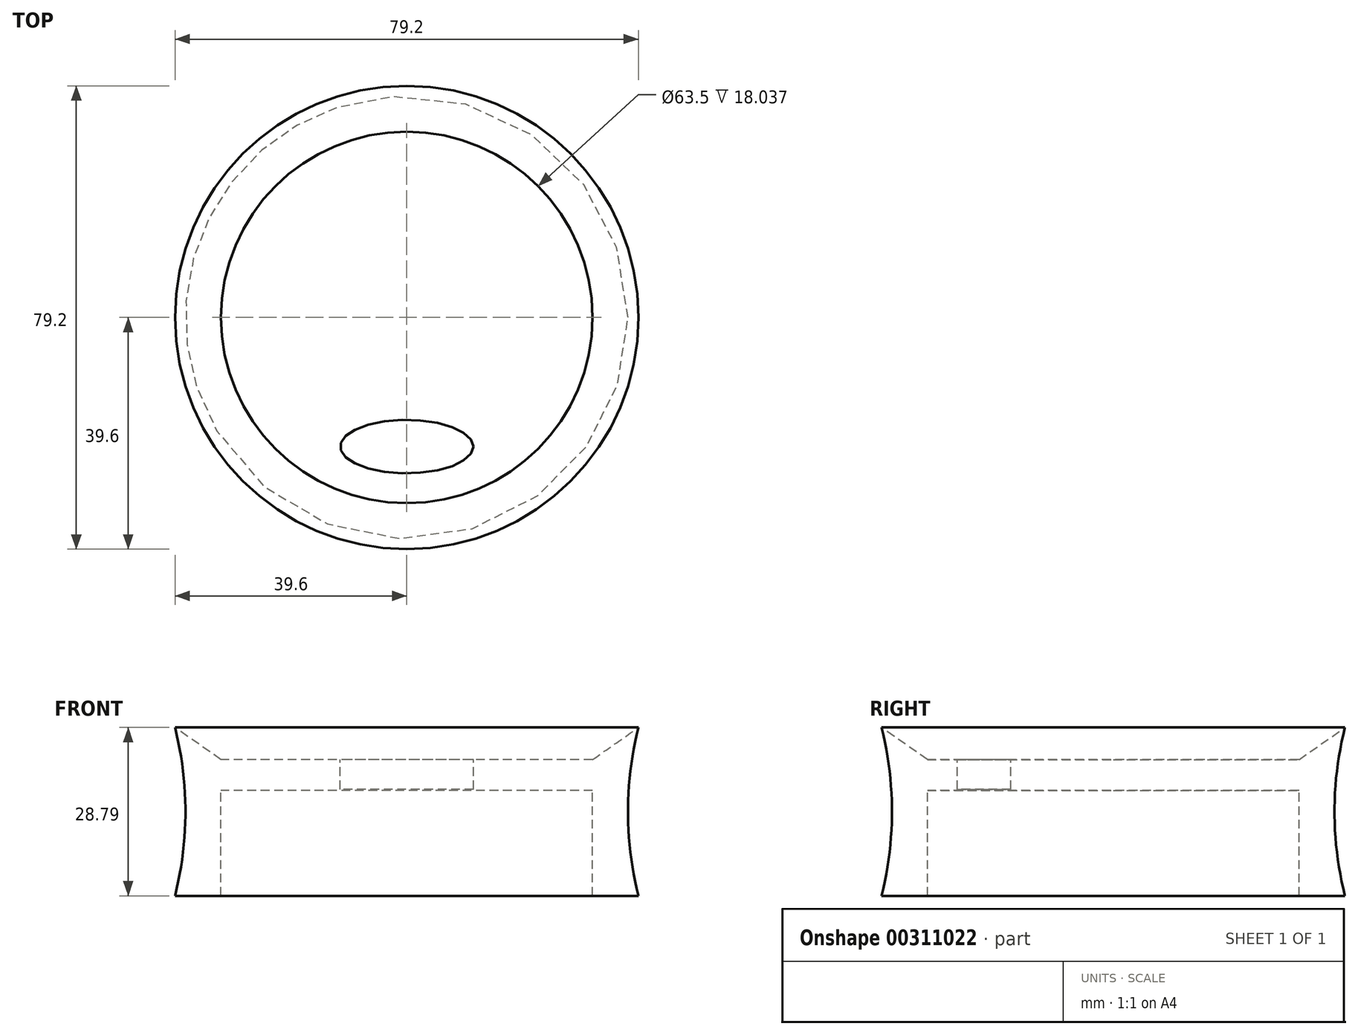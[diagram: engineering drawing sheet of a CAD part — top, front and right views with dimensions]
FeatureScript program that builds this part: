
annotation { "Feature Type Name" : "Feature", "Feature Type Description" : "" }
export const myFeature = defineFeature(function(context is Context, id is Id, definition is map)
    precondition{}
    {
        {
            var Q0;
            Q0=qCreatedBy(makeId("Front.planeOp"),FACE);
            var sketch = newSketch(context, id + "F0", { "sketchPlane" : qUnion([Q0])});
            skLineSegment(sketch, "E0", {"start": v(0, 14.52) * mm, "end": v(39.6, 14.52) * mm});
            skLineSegment(sketch, "E1", {"start": v(39.6, -14.27) * mm, "end": v(0, -14.27) * mm});
            skLineSegment(sketch, "E2", {"start": v(31.75, 9) * mm, "end": v(39.6, 14.52) * mm});
            skLineSegment(sketch, "E3", {"start": v(31.75, 9) * mm, "end": v(0, 9) * mm});
            skLineSegment(sketch, "E4", {"start": v(31.75, 3.77) * mm, "end": v(0, 3.77) * mm});
            skLineSegment(sketch, "E5", {"start": v(31.75, 3.77) * mm, "end": v(31.75, -14.27) * mm});
            skLineSegment(sketch, "E6", {"start": v(0, 14.52) * mm, "end": v(0, -14.27) * mm});
            skArc(sketch, "E7", {"start": v(39.6, 14.52) * mm, "mid": v(37.82, 0.13) * mm, "end": v(39.6, -14.27) * mm});
            skSolve(sketch);
        }
        {
            var Q0;
            Q0=makeQuery(id+"F0.imprint","IMPRINT",FACE,{"disambiguationData":[TD([[makeQuery(id+"F0.imprint","IMPRINT",EDGE,{"derivedFrom":sQuery(id+"F0.wireOp",EDGE,"E2")}),-1.0]])]});
            var Q1;
            Q1=sQuery(id+"F0.wireOp",EDGE,"E6");
            revolve(context, id + "F1", {"entities" : qUnion([Q0]), "axis" : qUnion([Q1]), "revolveType" : RevolveType.FULL});
        }
        {
            var Q0;
            Q0=makeQuery(id+"F1.opRevolve","SWEPT_FACE",FACE,{"disambiguationData":[OSD([sQuery(id+"F0.wireOp",EDGE,"E3")])]});
            var sketch = newSketch(context, id + "F2", { "sketchPlane" : qUnion([Q0])});
            skEllipse(sketch, "E8", {"center": v(0, -22.09) * mm, "majorRadius": 11.39 * mm, "minorRadius": 4.56 * mm, "majorAxis": v(1, 0)});
            skSolve(sketch);
        }
        {
            var Q0;
            Q0=makeQuery(id+"F2.imprint","IMPRINT",FACE,{"disambiguationData":[TD([[makeQuery(id+"F2.imprint","IMPRINT",EDGE,{"derivedFrom":sQuery(id+"F2.wireOp",EDGE,"E8")}),1.0]])]});
            extrude(context, id + "F3", {"entities" : qUnion([Q0]), "operationType" : NewBodyOperationType.REMOVE, "oppositeDirection" : true, "depth" : 5.08 * mm});
        }
    });
